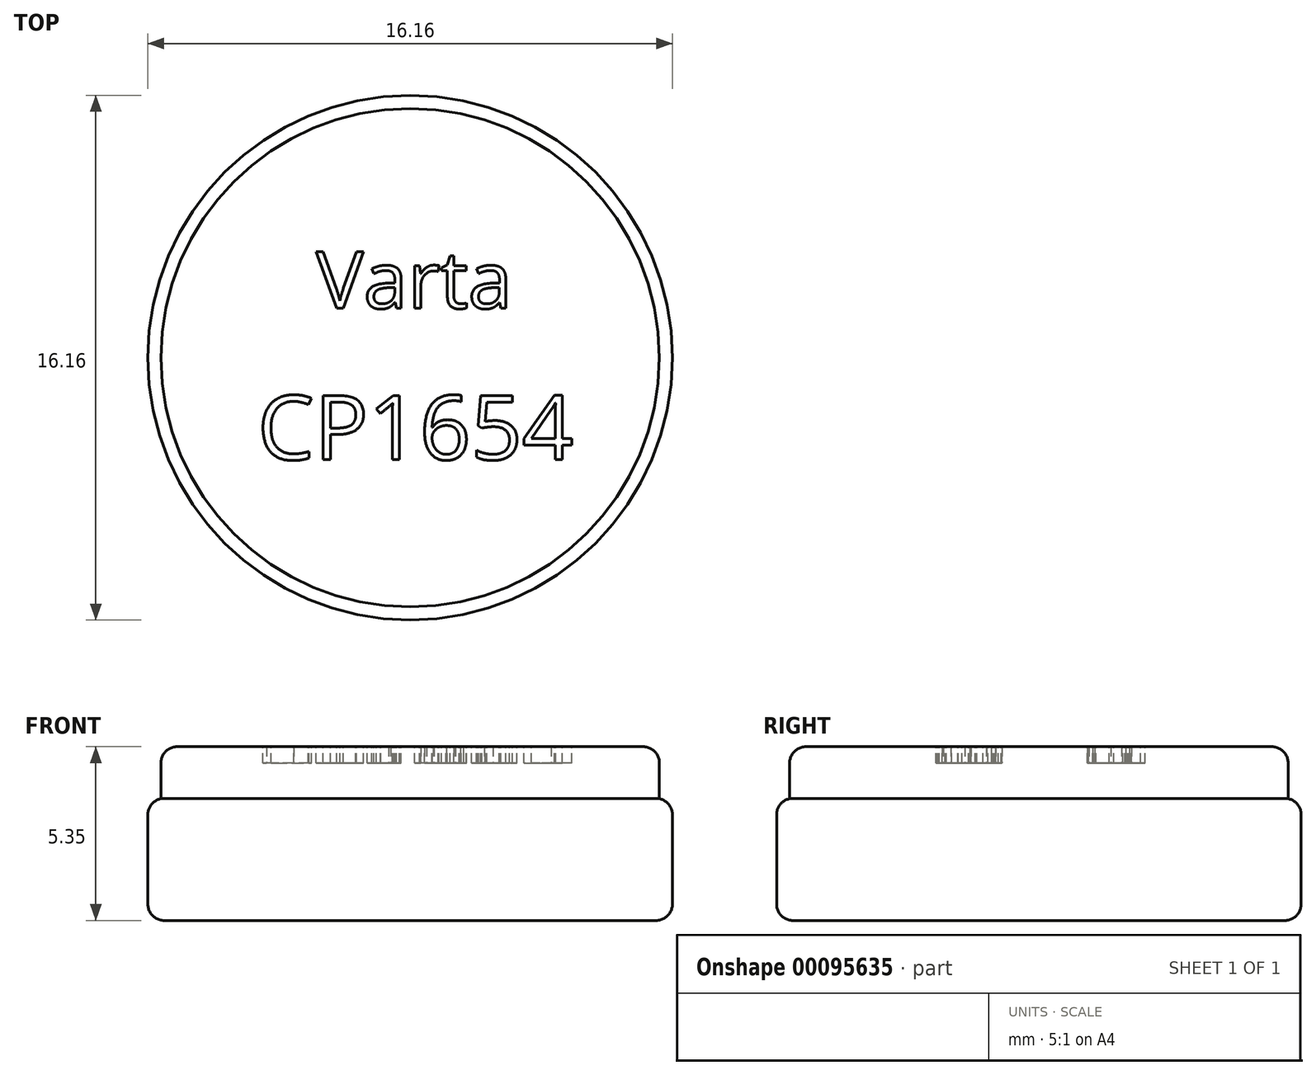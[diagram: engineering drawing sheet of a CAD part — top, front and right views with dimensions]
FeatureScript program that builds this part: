
annotation { "Feature Type Name" : "Feature", "Feature Type Description" : "" }
export const myFeature = defineFeature(function(context is Context, id is Id, definition is map)
    precondition{}
    {
        {
            var Q0;
            Q0=qCreatedBy(makeId("Top.planeOp"),FACE);
            var sketch = newSketch(context, id + "F0", { "sketchPlane" : qUnion([Q0])});
            skCircle(sketch, "E0", {"center": v(0, 0) * mm, "radius": 7.68 * mm});
            skSolve(sketch);
        }
        {
            var Q0;
            Q0=qSketchRegion(id+"F0",true);
            extrude(context, id + "F1", {"entities" : qUnion([Q0]), "depth" : 1.6 * mm});
        }
        {
            var Q0;
            Q0=makeQuery(id+"F1.opExtrude","CAP_FACE",FACE,{"disambiguationData":[OSD([sQuery(id+"F0.wireOp",EDGE,"E0")])],"isStart":false});
            var sketch = newSketch(context, id + "F2", { "sketchPlane" : qUnion([Q0])});
            skText(sketch, "E1", { "text": "Varta", "fontName": "OpenSans-Regular.ttf"});
            skText(sketch, "E2", { "text": "CP1654\n      --      \n", "fontName": "OpenSans-Regular.ttf"});
            const initialGuessF2  = {"E1": [-0.00289, 0.00152, 1, 0, 0.00176], "E2": [-0.0047, -0.00314, 1, 0, 0.00199]};
            skSetInitialGuess(sketch, initialGuessF2);
            skSolve(sketch);
        }
        {
            var Q0;
            Q0=makeQuery(id+"F2.imprint","IMPRINT",FACE,{"disambiguationData":[TD([[makeQuery(id+"F2.imprint","IMPRINT",EDGE,{"derivedFrom":sQuery(id+"F2.wireOp",EDGE,"E1.sketch_text.stroke-0")}),-1.0]])]});
            var Q1;
            Q1=makeQuery(id+"F2.imprint","IMPRINT",FACE,{"disambiguationData":[TD([[makeQuery(id+"F2.imprint","IMPRINT",EDGE,{"derivedFrom":sQuery(id+"F2.wireOp",EDGE,"E1.sketch_text.stroke-36")}),-1.0]])]});
            var Q2;
            Q2=makeQuery(id+"F2.imprint","IMPRINT",FACE,{"disambiguationData":[TD([[makeQuery(id+"F2.imprint","IMPRINT",EDGE,{"derivedFrom":sQuery(id+"F2.wireOp",EDGE,"E1.sketch_text.stroke-49")}),-1.0]])]});
            var Q3;
            Q3=makeQuery(id+"F2.imprint","IMPRINT",FACE,{"disambiguationData":[TD([[makeQuery(id+"F2.imprint","IMPRINT",EDGE,{"derivedFrom":sQuery(id+"F2.wireOp",EDGE,"E2.sketch_text.stroke-0")}),-1.0]])]});
            var Q4;
            Q4=makeQuery(id+"F2.imprint","IMPRINT",FACE,{"disambiguationData":[TD([[makeQuery(id+"F2.imprint","IMPRINT",EDGE,{"derivedFrom":sQuery(id+"F2.wireOp",EDGE,"E2.sketch_text.stroke-30")}),-1.0]])]});
            var Q5;
            Q5=makeQuery(id+"F2.imprint","IMPRINT",FACE,{"disambiguationData":[TD([[makeQuery(id+"F2.imprint","IMPRINT",EDGE,{"derivedFrom":sQuery(id+"F2.wireOp",EDGE,"E2.sketch_text.stroke-64")}),-1.0]])]});
            var Q6;
            Q6=makeQuery(id+"F2.imprint","IMPRINT",FACE,{"disambiguationData":[TD([[makeQuery(id+"F2.imprint","IMPRINT",EDGE,{"derivedFrom":sQuery(id+"F2.wireOp",EDGE,"E1.sketch_text.stroke-9")}),-1.0]])]});
            var Q7;
            Q7=makeQuery(id+"F2.imprint","IMPRINT",FACE,{"disambiguationData":[TD([[makeQuery(id+"F2.imprint","IMPRINT",EDGE,{"derivedFrom":sQuery(id+"F2.wireOp",EDGE,"E1.sketch_text.stroke-68")}),-1.0]])]});
            var Q8;
            Q8=makeQuery(id+"F2.imprint","IMPRINT",FACE,{"disambiguationData":[TD([[makeQuery(id+"F2.imprint","IMPRINT",EDGE,{"derivedFrom":sQuery(id+"F2.wireOp",EDGE,"E2.sketch_text.stroke-15")}),-1.0]])]});
            var Q9;
            Q9=makeQuery(id+"F2.imprint","IMPRINT",FACE,{"disambiguationData":[TD([[makeQuery(id+"F2.imprint","IMPRINT",EDGE,{"derivedFrom":sQuery(id+"F2.wireOp",EDGE,"E2.sketch_text.stroke-39")}),-1.0]])]});
            var Q10;
            Q10=makeQuery(id+"F2.imprint","IMPRINT",FACE,{"disambiguationData":[TD([[makeQuery(id+"F2.imprint","IMPRINT",EDGE,{"derivedFrom":sQuery(id+"F2.wireOp",EDGE,"E2.sketch_text.stroke-83")}),-1.0]])]});
            extrude(context, id + "F3", {"entities" : qUnion([Q0, Q1, Q2, Q3, Q4, Q5, Q6, Q7, Q8, Q9, Q10]), "operationType" : NewBodyOperationType.REMOVE, "oppositeDirection" : true, "depth" : .5 * mm});
        }
        {
            var Q0;
            Q0=makeQuery(id+"F1.opExtrude","CAP_FACE",FACE,{"disambiguationData":[OSD([sQuery(id+"F0.wireOp",EDGE,"E0")])],"isStart":true});
            var sketch = newSketch(context, id + "F4", { "sketchPlane" : qUnion([Q0])});
            skCircle(sketch, "E3", {"center": v(0, 0) * mm, "radius": 8.07 * mm});
            skSolve(sketch);
        }
        {
            var Q0;
            Q0=qSketchRegion(id+"F4",true);
            extrude(context, id + "F5", {"entities" : qUnion([Q0]), "operationType" : NewBodyOperationType.ADD, "depth" : 3.75 * mm});
        }
        {
            var Q0;
            Q0=makeQuery(id+"F1.opExtrude","CAP_EDGE",EDGE,{"disambiguationData":[OSD([sQuery(id+"F0.wireOp",EDGE,"E0")])],"isStart":false});
            var Q1;
            Q1=makeQuery(id+"F5.opExtrude","CAP_EDGE",EDGE,{"disambiguationData":[OSD([sQuery(id+"F4.wireOp",EDGE,"E3")])],"isStart":true});
            var Q2;
            Q2=makeQuery(id+"F5.opExtrude","CAP_EDGE",EDGE,{"disambiguationData":[OSD([sQuery(id+"F4.wireOp",EDGE,"E3")])],"isStart":false});
            fillet(context, id + "F6", {"entities" : qUnion([Q0, Q1, Q2]), "radius" : .5 * mm, "tangentPropagation" : true, "allowEdgeOverflow" : false});
        }
    });
